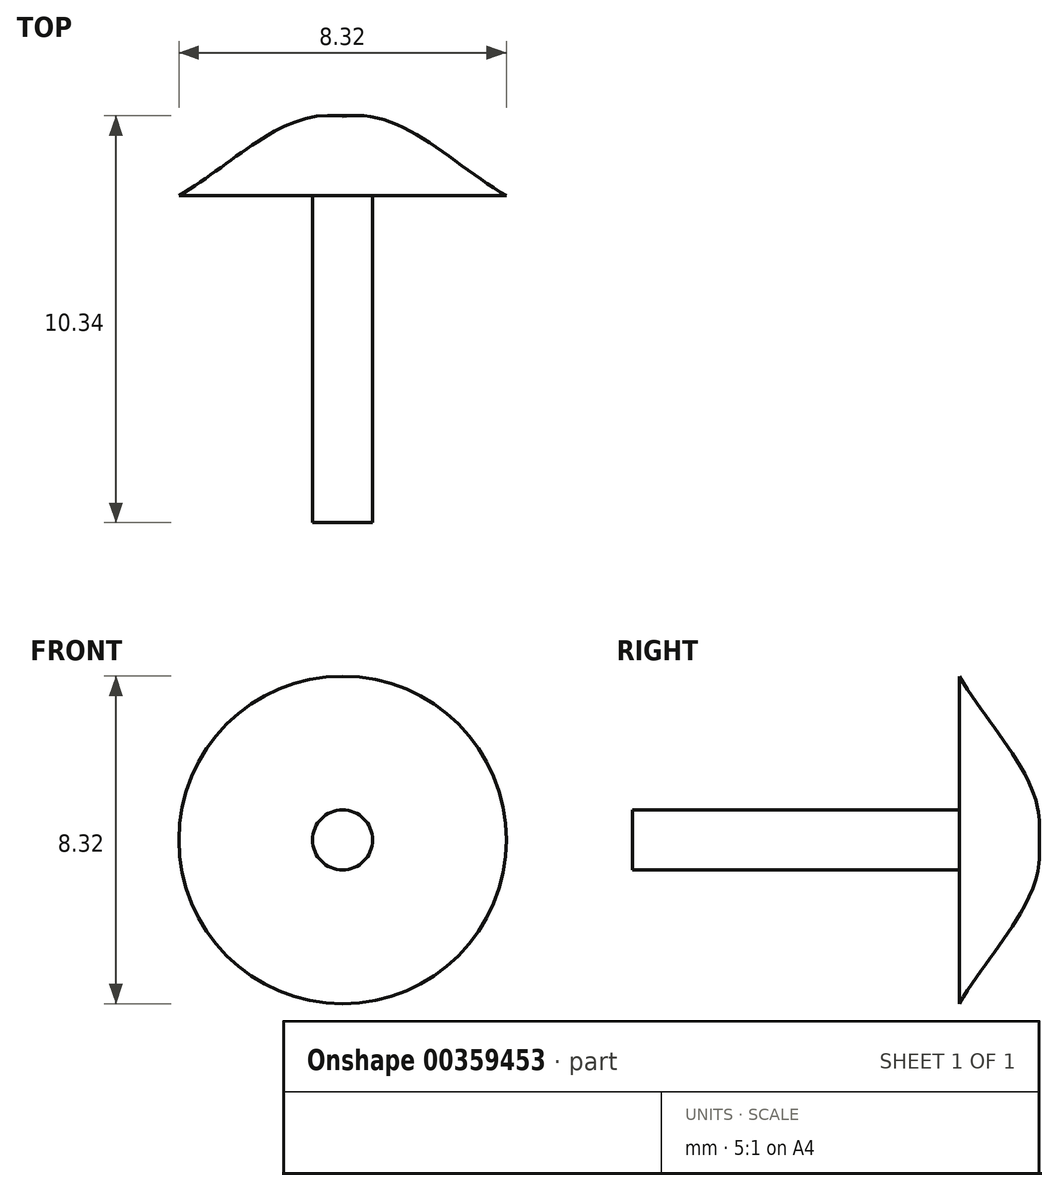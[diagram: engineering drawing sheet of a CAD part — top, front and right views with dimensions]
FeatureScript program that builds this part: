
annotation { "Feature Type Name" : "Feature", "Feature Type Description" : "" }
export const myFeature = defineFeature(function(context is Context, id is Id, definition is map)
    precondition{}
    {
        {
            var Q0;
            Q0=qCreatedBy(makeId("Top.planeOp"),FACE);
            var sketch = newSketch(context, id + "F0", { "sketchPlane" : qUnion([Q0])});
            skLineSegment(sketch, "E0.bottom", {"start": v(-3.55, 0) * mm, "end": v(-2.03, 0) * mm});
            skLineSegment(sketch, "E0.top", {"start": v(-3.55, -8.3) * mm, "end": v(-2.03, -8.3) * mm});
            skLineSegment(sketch, "E0.left", {"start": v(-3.55, 0) * mm, "end": v(-3.55, -8.3) * mm});
            skLineSegment(sketch, "E0.right", {"start": v(-2.03, 0) * mm, "end": v(-2.03, -8.3) * mm});
            skLineSegment(sketch, "E1", {"start": v(-3.55, 0) * mm, "end": v(-6.5, 0) * mm});
            skLineSegment(sketch, "E2", {"start": v(-2.03, 0) * mm, "end": v(1.37, 0) * mm});
            skFitSpline(sketch, "E3", {"points": [v(-6.5, 0) * mm, v(-2.35, 2.03) * mm, v(1.37, 0) * mm], "startDerivative": vector(8.24, 4.22) * mm, "endDerivative": vector(7.5, -4.3) * mm});
            skLineSegment(sketch, "E4", {"start": v(-2.8, -8.3) * mm, "end": v(-2.8, 6.37) * mm, "construction": true});
            skLineSegment(sketch, "E5", {"start": v(-2.8, -8.3) * mm, "end": v(-2.8, 3.03) * mm});
            skSolve(sketch);
        }
        {
            var Q0;
            {var subQ0=sQuery(id+"F0.wireOp",EDGE,"E2");Q0=makeQuery(id+"F0.imprint","IMPRINT",FACE,{"disambiguationData":[TD([[makeQuery(id+"F0.imprint","IMPRINT",EDGE,{"derivedFrom":subQ0}),1.0]])]});}
            var Q1;
            {var subQ0=sQuery(id+"F0.wireOp",EDGE,"E0.right");Q1=makeQuery(id+"F0.imprint","IMPRINT",FACE,{"disambiguationData":[TD([[makeQuery(id+"F0.imprint","IMPRINT",EDGE,{"derivedFrom":subQ0}),-1.0]])]});}
            var Q2;
            Q2=sQuery(id+"F0.wireOp",EDGE,"E4");
            revolve(context, id + "F1", {"entities" : qUnion([Q0, Q1]), "axis" : qUnion([Q2]), "revolveType" : RevolveType.FULL});
        }
    });
